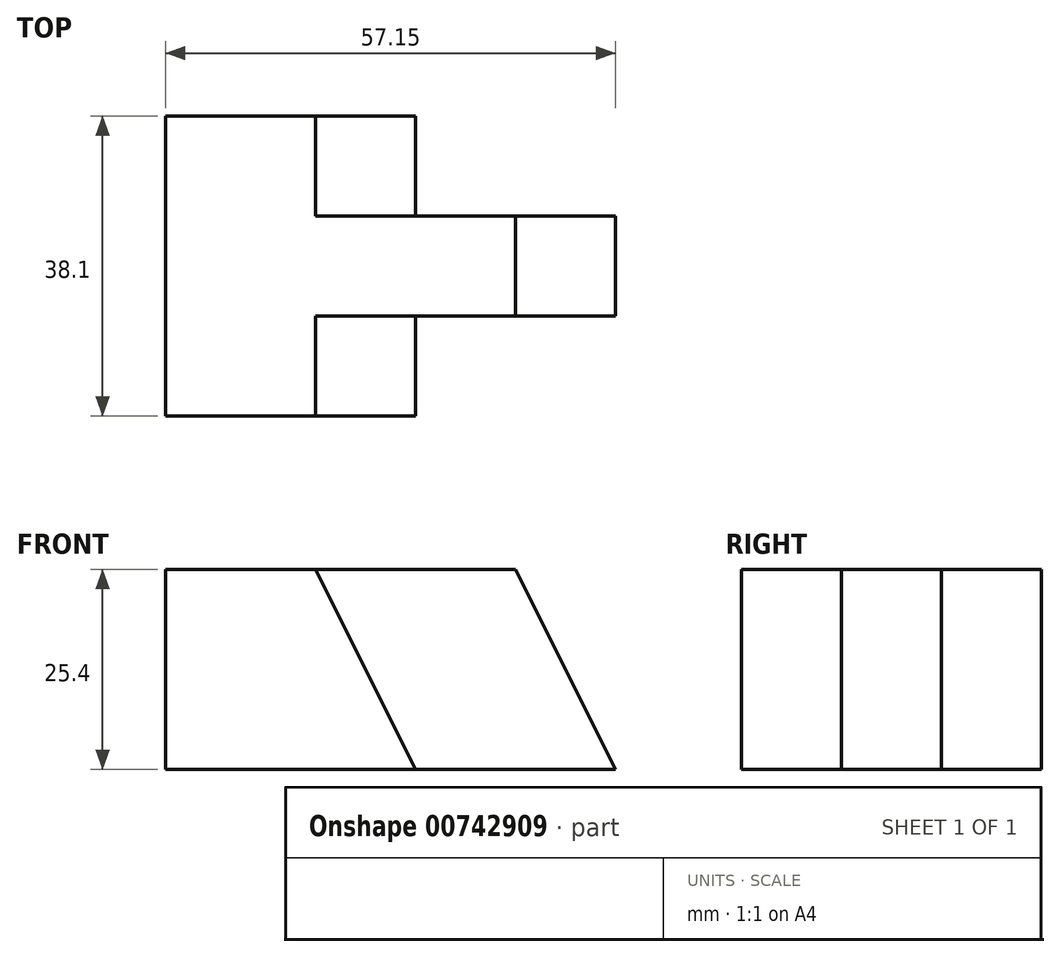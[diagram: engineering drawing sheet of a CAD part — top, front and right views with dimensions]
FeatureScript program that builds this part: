
annotation { "Feature Type Name" : "Feature", "Feature Type Description" : "" }
export const myFeature = defineFeature(function(context is Context, id is Id, definition is map)
    precondition{}
    {
        {
            var Q0;
            Q0=qCreatedBy(makeId("Top.planeOp"),FACE);
            var sketch = newSketch(context, id + "F0", { "sketchPlane" : qUnion([Q0])});
            skLineSegment(sketch, "E0", {"start": v(0, 0) * mm, "end": v(19.05, 0) * mm});
            skLineSegment(sketch, "E1", {"start": v(19.05, 0) * mm, "end": v(19.05, 12.7) * mm});
            skLineSegment(sketch, "E2", {"start": v(19.05, 12.7) * mm, "end": v(44.45, 12.7) * mm});
            skLineSegment(sketch, "E3", {"start": v(44.45, 12.7) * mm, "end": v(44.45, 25.4) * mm});
            skLineSegment(sketch, "E4", {"start": v(44.45, 25.4) * mm, "end": v(19.05, 25.4) * mm});
            skLineSegment(sketch, "E5", {"start": v(19.05, 25.4) * mm, "end": v(19.05, 38.1) * mm});
            skLineSegment(sketch, "E6", {"start": v(19.05, 38.1) * mm, "end": v(0, 38.1) * mm});
            skLineSegment(sketch, "E7", {"start": v(0, 38.1) * mm, "end": v(0, 0) * mm});
            skSolve(sketch);
        }
        {
            var Q0;
            Q0=makeQuery(id+"F0.imprint","IMPRINT",FACE,{"disambiguationData":[TD([[makeQuery(id+"F0.imprint","IMPRINT",EDGE,{"derivedFrom":sQuery(id+"F0.wireOp",EDGE,"E0")}),1.0]])]});
            extrude(context, id + "F1", {"entities" : qUnion([Q0]), "depth" : 25.4 * mm, "offsetDistance" : 25.4 * mm});
        }
        {
            var Q0;
            Q0=makeQuery(id+"F1.opExtrude","SWEPT_FACE",FACE,{"disambiguationData":[OSD([sQuery(id+"F0.wireOp",EDGE,"E2")])]});
            var sketch = newSketch(context, id + "F2", { "sketchPlane" : qUnion([Q0])});
            skLineSegment(sketch, "E8", {"start": v(19.05, 25.4) * mm, "end": v(31.75, 0) * mm});
            skLineSegment(sketch, "E9", {"start": v(31.75, 0) * mm, "end": v(19.05, 0) * mm});
            skLineSegment(sketch, "E10", {"start": v(19.05, 0) * mm, "end": v(19.05, 25.4) * mm});
            skSolve(sketch);
        }
        {
            var Q0;
            Q0=makeQuery(id+"F2.imprint","IMPRINT",FACE,{"disambiguationData":[TD([[makeQuery(id+"F2.imprint","IMPRINT",EDGE,{"derivedFrom":sQuery(id+"F2.wireOp",EDGE,"E8")}),-1.0]])]});
            extrude(context, id + "F3", {"entities" : qUnion([Q0]), "operationType" : NewBodyOperationType.ADD, "depth" : 12.7 * mm, "offsetDistance" : 25.4 * mm});
        }
        {
            var Q0;
            Q0=makeQuery(id+"F1.opExtrude","SWEPT_FACE",FACE,{"disambiguationData":[OSD([sQuery(id+"F0.wireOp",EDGE,"E2")])]});
            var sketch = newSketch(context, id + "F4", { "sketchPlane" : qUnion([Q0])});
            skLineSegment(sketch, "E11", {"start": v(44.45, 25.4) * mm, "end": v(57.15, 0) * mm});
            skLineSegment(sketch, "E12", {"start": v(57.15, 0) * mm, "end": v(44.45, 0) * mm});
            skLineSegment(sketch, "E13", {"start": v(44.45, 0) * mm, "end": v(44.45, 25.4) * mm});
            skSolve(sketch);
        }
        {
            var Q0;
            Q0=makeQuery(id+"F4.imprint","IMPRINT",FACE,{"disambiguationData":[TD([[makeQuery(id+"F4.imprint","IMPRINT",EDGE,{"derivedFrom":sQuery(id+"F4.wireOp",EDGE,"E11")}),-1.0]])]});
            extrude(context, id + "F5", {"entities" : qUnion([Q0]), "operationType" : NewBodyOperationType.ADD, "oppositeDirection" : true, "depth" : 12.7 * mm, "offsetDistance" : 25.4 * mm});
        }
        {
            var Q0;
            Q0=makeQuery(id+"F5.boolean.opBoolean","MERGE",FACE,{"derivedFrom":[makeQuery(id+"F1.opExtrude","SWEPT_FACE",FACE,{"disambiguationData":[OSD([sQuery(id+"F0.wireOp",EDGE,"E4")])]}),makeQuery(id+"F5.opExtrude","CAP_FACE",FACE,{"disambiguationData":[OSD([sQuery(id+"F4.wireOp",EDGE,"E11"),sQuery(id+"F4.wireOp",EDGE,"E12"),sQuery(id+"F4.wireOp",EDGE,"E13")])],"isStart":false})]});
            var sketch = newSketch(context, id + "F6", { "sketchPlane" : qUnion([Q0])});
            skLineSegment(sketch, "E14", {"start": v(-19.05, 25.4) * mm, "end": v(-19.05, 0) * mm});
            skLineSegment(sketch, "E15", {"start": v(-19.05, 0) * mm, "end": v(-31.75, 0) * mm});
            skLineSegment(sketch, "E16", {"start": v(-31.75, 0) * mm, "end": v(-19.05, 25.4) * mm});
            skSolve(sketch);
        }
        {
            var Q0;
            Q0=makeQuery(id+"F6.imprint","IMPRINT",FACE,{"disambiguationData":[TD([[makeQuery(id+"F6.imprint","IMPRINT",EDGE,{"derivedFrom":sQuery(id+"F6.wireOp",EDGE,"E14")}),-1.0]])]});
            extrude(context, id + "F7", {"entities" : qUnion([Q0]), "operationType" : NewBodyOperationType.ADD, "depth" : 12.7 * mm, "offsetDistance" : 25.4 * mm});
        }
    });
